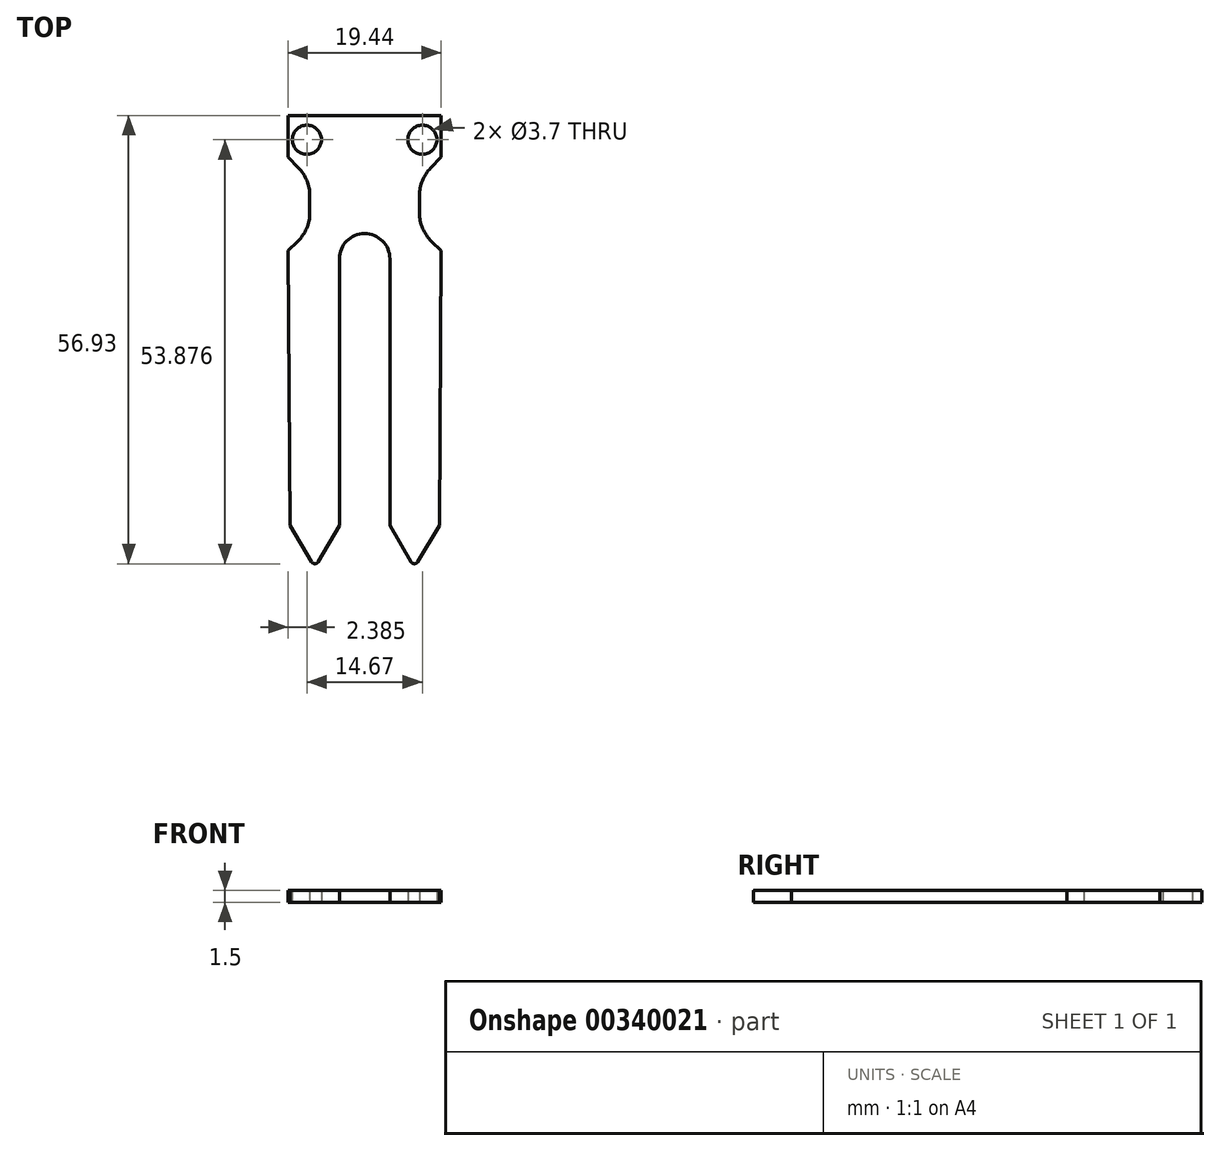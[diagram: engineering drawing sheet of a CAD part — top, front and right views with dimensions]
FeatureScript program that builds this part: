
annotation { "Feature Type Name" : "Feature", "Feature Type Description" : "" }
export const myFeature = defineFeature(function(context is Context, id is Id, definition is map)
    precondition{}
    {
        {
            var Q0;
            Q0=qCreatedBy(makeId("Top.planeOp"),FACE);
            var sketch = newSketch(context, id + "F0", { "sketchPlane" : qUnion([Q0])});
            skLineSegment(sketch, "E0", {"start": v(0, 0) * mm, "end": v(9.72, 0) * mm});
            skLineSegment(sketch, "E1", {"start": v(9.72, 0) * mm, "end": v(9.72, -5.28) * mm});
            skLineSegment(sketch, "E2", {"start": v(9.73, -5.28) * mm, "end": v(8.39, -6.65) * mm});
            skLineSegment(sketch, "E3", {"start": v(6.96, -10.14) * mm, "end": v(6.96, -12.36) * mm});
            skLineSegment(sketch, "E4", {"start": v(8.51, -15.97) * mm, "end": v(9.73, -17.13) * mm});
            skLineSegment(sketch, "E5", {"start": v(9.49, -52.08) * mm, "end": v(6.31, -57.42) * mm});
            skLineSegment(sketch, "E6", {"start": v(6.31, -57.42) * mm, "end": v(3.2, -52.04) * mm});
            skLineSegment(sketch, "E7", {"start": v(3.2, -52.04) * mm, "end": v(9.49, -52.04) * mm});
            skLineSegment(sketch, "E8", {"start": v(9.73, -17.13) * mm, "end": v(9.49, -52.08) * mm});
            skLineSegment(sketch, "E9", {"start": v(3.2, -52.04) * mm, "end": v(3.2, -18.2) * mm});
            skLineSegment(sketch, "E10", {"start": v(0, 28.18) * mm, "end": v(0, -60.85) * mm});
            skLineSegment(sketch, "E11.MirrorCS", {"start": v(-9.72, 0) * mm, "end": v(-9.72, -5.28) * mm});
            skLineSegment(sketch, "E12.MirrorCS", {"start": v(0, 0) * mm, "end": v(-9.72, 0) * mm});
            skLineSegment(sketch, "E13.MirrorCS", {"start": v(-9.73, -5.28) * mm, "end": v(-8.39, -6.65) * mm});
            skLineSegment(sketch, "E14.MirrorCS", {"start": v(-6.96, -10.14) * mm, "end": v(-6.96, -12.36) * mm});
            skLineSegment(sketch, "E15.MirrorCS", {"start": v(-8.51, -15.97) * mm, "end": v(-9.73, -17.13) * mm});
            skLineSegment(sketch, "E16.MirrorCS", {"start": v(-9.73, -17.13) * mm, "end": v(-9.49, -52.08) * mm});
            skLineSegment(sketch, "E17.MirrorCS", {"start": v(-3.2, -52.04) * mm, "end": v(-3.2, -18.2) * mm});
            skLineSegment(sketch, "E18.MirrorCS", {"start": v(-6.31, -57.42) * mm, "end": v(-3.2, -52.04) * mm});
            skLineSegment(sketch, "E19.MirrorCS", {"start": v(-9.49, -52.08) * mm, "end": v(-6.31, -57.42) * mm});
            skLineSegment(sketch, "E20.MirrorCS", {"start": v(-3.2, -52.04) * mm, "end": v(-9.49, -52.04) * mm});
            skArc(sketch, "E21", {"start": v(3.2, -18.2) * mm, "mid": v(0, -14.99) * mm, "end": v(-3.2, -18.2) * mm});
            skPoint(sketch, "E22.visualSharp", {"position": v(6.96, -8.1) * mm});
            skArc(sketch, "E22.filletArc", {"start": v(8.39, -6.65) * mm, "mid": v(7.33, -8.25) * mm, "end": v(6.96, -10.14) * mm});
            skPoint(sketch, "E23.visualSharp", {"position": v(6.97, -14.5) * mm});
            skArc(sketch, "E23.filletArc", {"start": v(6.96, -12.36) * mm, "mid": v(7.37, -14.32) * mm, "end": v(8.51, -15.97) * mm});
            skPoint(sketch, "E24.visualSharp", {"position": v(-6.96, -14.5) * mm});
            skArc(sketch, "E24.filletArc", {"start": v(-8.51, -15.97) * mm, "mid": v(-7.37, -14.32) * mm, "end": v(-6.96, -12.36) * mm});
            skPoint(sketch, "E25.visualSharp", {"position": v(-6.96, -8.1) * mm});
            skArc(sketch, "E25.filletArc", {"start": v(-6.96, -10.14) * mm, "mid": v(-7.33, -8.25) * mm, "end": v(-8.39, -6.65) * mm});
            skCircle(sketch, "E26", {"center": v(-7.33, -3.05) * mm, "radius": 1.85 * mm});
            skPoint(sketch, "E26.centerSnap0", {"position": v(-7.33, -8.25) * mm});
            skCircle(sketch, "E27.MirrorC", {"center": v(7.33, -3.05) * mm, "radius": 1.85 * mm});
            skSolve(sketch);
        }
        {
            var Q0;
            Q0 = qSketchRegion(id + "F0", true);
            extrude(context, id + "F1", {"entities" : qUnion([Q0]), "depth" : 1.5 * mm});
        }
        {
            var Q0;
            Q0=makeQuery(id+"F1.opExtrude","SWEPT_EDGE",EDGE,{"disambiguationData":[OSD([sQuery(id+"F0.wireOp",EDGE,"E18.MirrorCS"),sQuery(id+"F0.wireOp",EDGE,"E19.MirrorCS")])]});
            var Q1;
            Q1=makeQuery(id+"F1.opExtrude","SWEPT_EDGE",EDGE,{"disambiguationData":[OSD([sQuery(id+"F0.wireOp",EDGE,"E5"),sQuery(id+"F0.wireOp",EDGE,"E6")])]});
            fillet(context, id + "F2", {"entities" : qUnion([Q0, Q1]), "radius" : .5 * mm, "tangentPropagation" : true, "allowEdgeOverflow" : false});
        }
    });
